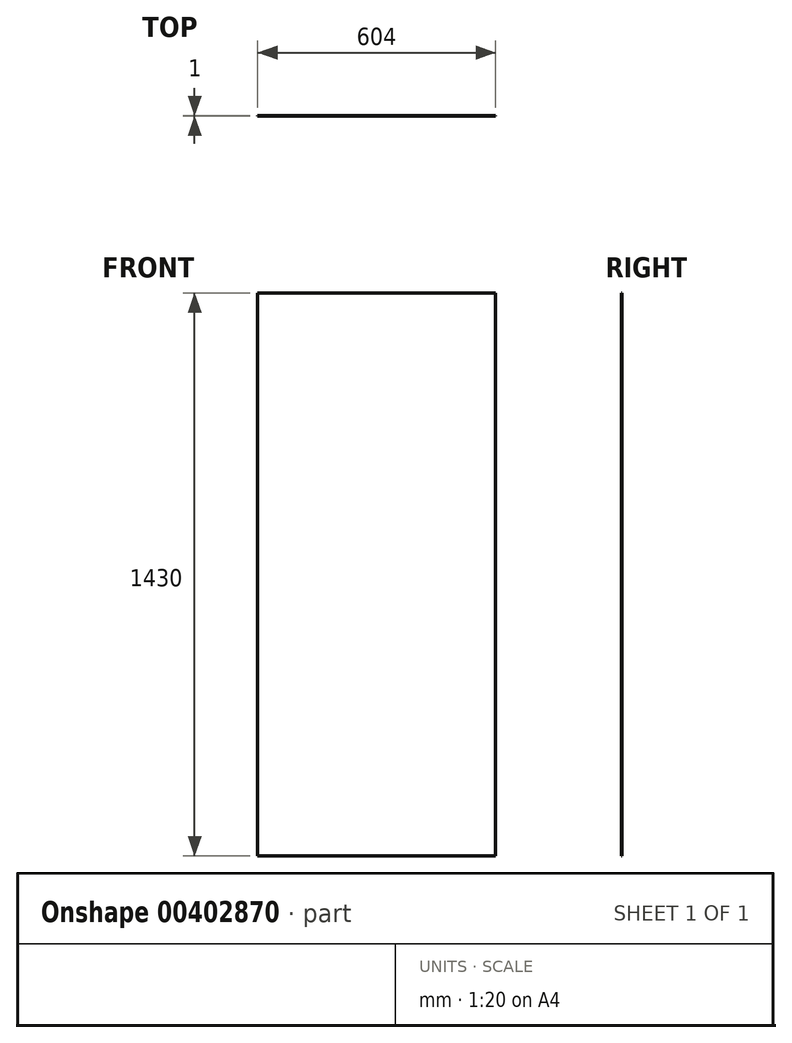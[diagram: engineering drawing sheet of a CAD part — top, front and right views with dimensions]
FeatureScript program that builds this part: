
annotation { "Feature Type Name" : "Feature", "Feature Type Description" : "" }
export const myFeature = defineFeature(function(context is Context, id is Id, definition is map)
    precondition{}
    {
        {
            var Q0;
            Q0=qCreatedBy(makeId("Front.planeOp"),FACE);
            var sketch = newSketch(context, id + "F0", { "sketchPlane" : qUnion([Q0])});
            skLineSegment(sketch, "E0.bottom", {"start": v(-302, 715) * mm, "end": v(302, 715) * mm});
            skLineSegment(sketch, "E0.top", {"start": v(-302, -715) * mm, "end": v(302, -715) * mm});
            skLineSegment(sketch, "E0.left", {"start": v(-302, 715) * mm, "end": v(-302, -715) * mm});
            skLineSegment(sketch, "E0.right", {"start": v(302, 715) * mm, "end": v(302, -715) * mm});
            skPoint(sketch, "E0.middle", {"position": v(0, 0) * mm});
            skSolve(sketch);
        }
        {
            var Q0;
            Q0=makeQuery(id+"F0.imprint","IMPRINT",FACE,{"disambiguationData":[TD([[makeQuery(id+"F0.imprint","IMPRINT",EDGE,{"derivedFrom":sQuery(id+"F0.wireOp",EDGE,"E0.bottom")}),-1.0]])]});
            extrude(context, id + "F1", {"entities" : qUnion([Q0]), "depth" : 1 * mm});
        }
    });
